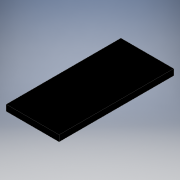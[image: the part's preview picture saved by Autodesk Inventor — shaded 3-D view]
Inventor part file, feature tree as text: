
AUTODESK INVENTOR PART (.ipt)
format: ipt  version: 2018 (Build 220112000, 112)  size: 133,120 bytes
history: native  units: in
note: dims shown in document units (in); Inventor stores cm internally (conversion verified against a paired STEP export)
features: extrude x3, sketch x3, fillet x2
ambient origin geometry x8: Origin, YZ Plane, XZ Plane, XY Plane, X Axis, Y Axis, Z Axis, Center Point
bodies: Solid1 (feature_tree)
feature tree (8):
  extrude  "Extrusion1"  Depth=21.6929in
  extrude  "Extrusion2"  Depth=0.125in
  fillet  "Fillet1"  Radius=0.125in
  extrude  "Extrusion3"  Depth=20.0in
  fillet  "Fillet2"  Radius=4.0in
  sketch  "Sketch1"  dims[d0=47.0866in d1=21.6929in]
  sketch  "Sketch2"  dims[d2=0.5in d3=0.0in d4=0.125in d5=0.125in]
  sketch  "Sketch3"  dims[d6=2.0in d7=0.0in d8=20.0in d9=4.0in d10=1.9in d11=0.0in d12=2.0in]
